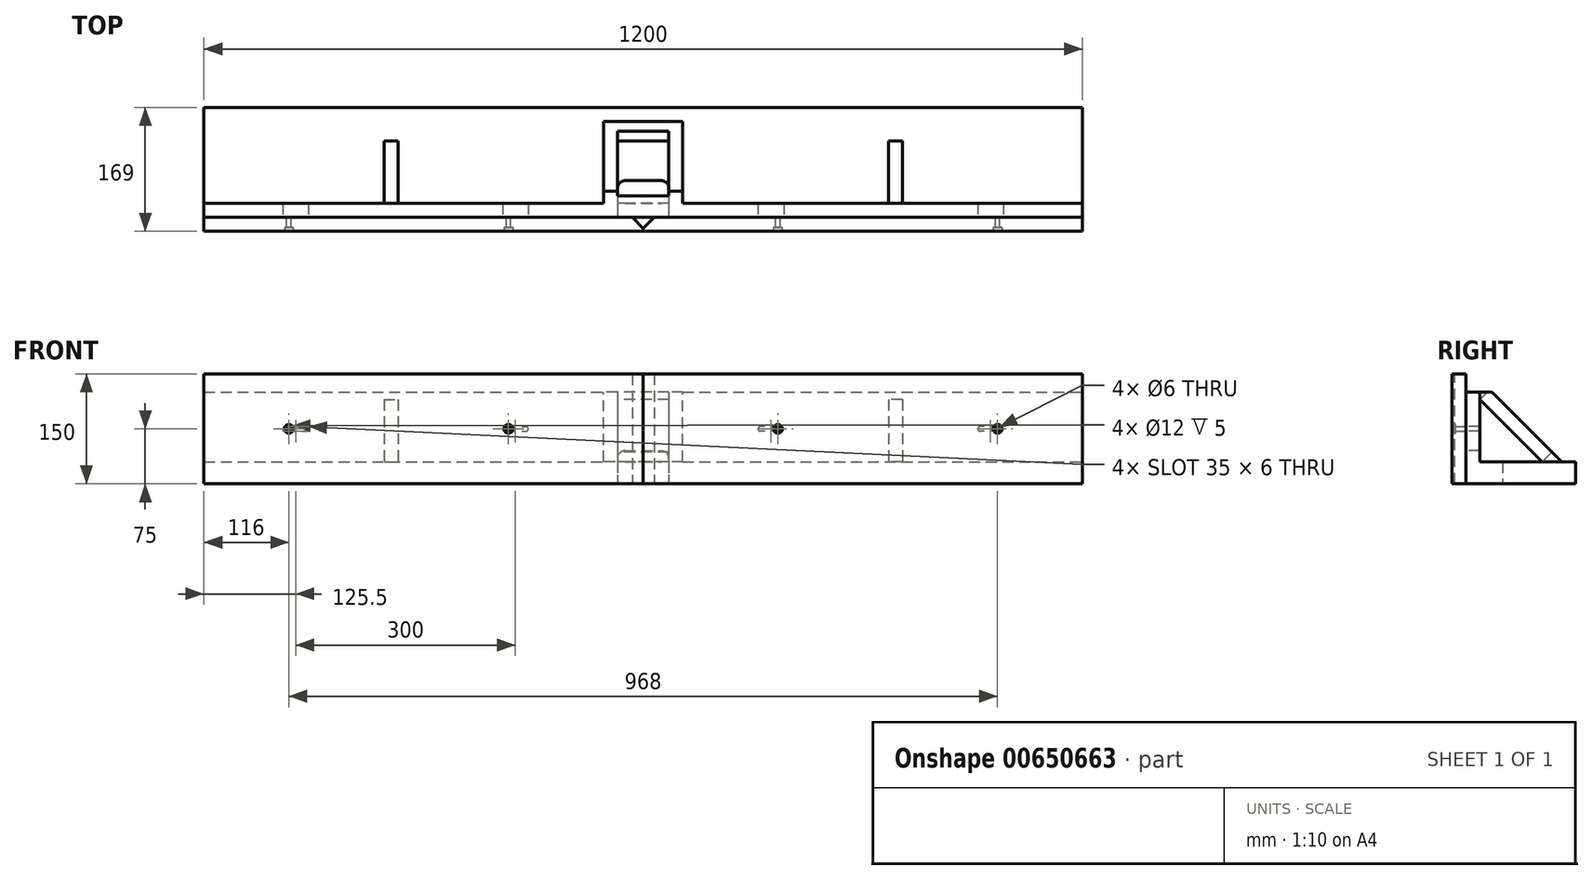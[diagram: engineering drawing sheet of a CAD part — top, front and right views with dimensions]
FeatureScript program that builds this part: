
annotation { "Feature Type Name" : "Feature", "Feature Type Description" : "" }
export const myFeature = defineFeature(function(context is Context, id is Id, definition is map)
    precondition{}
    {
        {
            var Q0;
            Q0=qCreatedBy(makeId("Front.planeOp"),FACE);
            var sketch = newSketch(context, id + "F0", { "sketchPlane" : qUnion([Q0])});
            skLineSegment(sketch, "E0.bottom", {"start": v(-600, 0) * mm, "end": v(600, 0) * mm});
            skLineSegment(sketch, "E0.top", {"start": v(-600, 125) * mm, "end": v(600, 125) * mm});
            skLineSegment(sketch, "E0.left", {"start": v(-600, 0) * mm, "end": v(-600, 125) * mm});
            skLineSegment(sketch, "E0.right", {"start": v(600, 0) * mm, "end": v(600, 125) * mm});
            skLineSegment(sketch, "E1.bottom", {"start": v(-25, 45) * mm, "end": v(25, 45) * mm});
            skLineSegment(sketch, "E1.top", {"start": v(-35, 0) * mm, "end": v(35, 0) * mm});
            skLineSegment(sketch, "E1.left", {"start": v(-35, 35) * mm, "end": v(-35, 0) * mm});
            skLineSegment(sketch, "E1.right", {"start": v(35, 35) * mm, "end": v(35, 0) * mm});
            skPoint(sketch, "E2.visualSharp", {"position": v(-35, 45) * mm});
            skArc(sketch, "E2.filletArc", {"start": v(-25, 45) * mm, "mid": v(-32.07, 42.07) * mm, "end": v(-35, 35) * mm});
            skPoint(sketch, "E3.visualSharp", {"position": v(35, 45) * mm});
            skArc(sketch, "E3.filletArc", {"start": v(35, 35) * mm, "mid": v(32.07, 42.07) * mm, "end": v(25, 45) * mm});
            skLineSegment(sketch, "E4", {"start": v(-574.08, 75) * mm, "end": v(534.24, 75) * mm, "construction": true});
            skLineSegment(sketch, "E5", {"start": v(-160, 105.56) * mm, "end": v(-160, 9.23) * mm, "construction": true});
            skLineSegment(sketch, "E6.bottom", {"start": v(-189, 78) * mm, "end": v(-160, 78) * mm});
            skLineSegment(sketch, "E6.top", {"start": v(-189, 72) * mm, "end": v(-160, 72) * mm});
            skLineSegment(sketch, "E6.left", {"start": v(-192, 75) * mm, "end": v(-192, 75) * mm});
            skLineSegment(sketch, "E6.right", {"start": v(-157, 75) * mm, "end": v(-157, 75) * mm});
            skPoint(sketch, "E7.visualSharp", {"position": v(-192, 78) * mm});
            skArc(sketch, "E7.filletArc", {"start": v(-189, 78) * mm, "mid": v(-191.12, 77.12) * mm, "end": v(-192, 75) * mm});
            skPoint(sketch, "E8.visualSharp", {"position": v(-192, 72) * mm});
            skArc(sketch, "E8.filletArc", {"start": v(-192, 75) * mm, "mid": v(-191.12, 72.88) * mm, "end": v(-189, 72) * mm});
            skPoint(sketch, "E9.visualSharp", {"position": v(-157, 78) * mm});
            skArc(sketch, "E9.filletArc", {"start": v(-157, 75) * mm, "mid": v(-157.88, 77.12) * mm, "end": v(-160, 78) * mm});
            skPoint(sketch, "E10.visualSharp", {"position": v(-157, 72) * mm});
            skArc(sketch, "E10.filletArc", {"start": v(-160, 72) * mm, "mid": v(-157.88, 72.88) * mm, "end": v(-157, 75) * mm});
            skPoint(sketch, "E11.1.0.0", {"position": v(-457, 78) * mm});
            skPoint(sketch, "E11.1.0.1", {"position": v(-492, 72) * mm});
            skLineSegment(sketch, "E11.1.0.2", {"start": v(-489, 78) * mm, "end": v(-460, 78) * mm});
            skPoint(sketch, "E11.1.0.3", {"position": v(-492, 78) * mm});
            skPoint(sketch, "E11.1.0.4", {"position": v(-457, 72) * mm});
            skLineSegment(sketch, "E11.1.0.5", {"start": v(-489, 72) * mm, "end": v(-460, 72) * mm});
            skArc(sketch, "E11.1.0.6", {"start": v(-492, 75) * mm, "mid": v(-491.12, 72.88) * mm, "end": v(-489, 72) * mm});
            skArc(sketch, "E11.1.0.7", {"start": v(-489, 78) * mm, "mid": v(-491.12, 77.12) * mm, "end": v(-492, 75) * mm});
            skArc(sketch, "E11.1.0.8", {"start": v(-457, 75) * mm, "mid": v(-457.88, 77.12) * mm, "end": v(-460, 78) * mm});
            skArc(sketch, "E11.1.0.9", {"start": v(-460, 72) * mm, "mid": v(-457.88, 72.88) * mm, "end": v(-457, 75) * mm});
            skLineSegment(sketch, "E11.direction1", {"start": v(-192, 72) * mm, "end": v(-492, 72) * mm, "construction": true});
            skArc(sketch, "E12.MirrorCS", {"start": v(157, 75) * mm, "mid": v(157.88, 77.12) * mm, "end": v(160, 78) * mm});
            skArc(sketch, "E13.MirrorCS", {"start": v(189, 78) * mm, "mid": v(191.12, 77.12) * mm, "end": v(192, 75) * mm});
            skArc(sketch, "E14.MirrorCS", {"start": v(160, 72) * mm, "mid": v(157.88, 72.88) * mm, "end": v(157, 75) * mm});
            skArc(sketch, "E15.MirrorCS", {"start": v(192, 75) * mm, "mid": v(191.12, 72.88) * mm, "end": v(189, 72) * mm});
            skPoint(sketch, "E16.MirrorP", {"position": v(192, 72) * mm});
            skPoint(sketch, "E17.MirrorP", {"position": v(192, 78) * mm});
            skLineSegment(sketch, "E18.MirrorCS", {"start": v(189, 72) * mm, "end": v(160, 72) * mm});
            skLineSegment(sketch, "E19.MirrorCS", {"start": v(189, 78) * mm, "end": v(160, 78) * mm});
            skPoint(sketch, "E20.MirrorP", {"position": v(157, 72) * mm});
            skPoint(sketch, "E21.MirrorP", {"position": v(157, 78) * mm});
            skArc(sketch, "E22.MirrorCS", {"start": v(457, 75) * mm, "mid": v(457.88, 77.12) * mm, "end": v(460, 78) * mm});
            skArc(sketch, "E23.MirrorCS", {"start": v(489, 78) * mm, "mid": v(491.12, 77.12) * mm, "end": v(492, 75) * mm});
            skArc(sketch, "E24.MirrorCS", {"start": v(492, 75) * mm, "mid": v(491.12, 72.88) * mm, "end": v(489, 72) * mm});
            skArc(sketch, "E25.MirrorCS", {"start": v(460, 72) * mm, "mid": v(457.88, 72.88) * mm, "end": v(457, 75) * mm});
            skPoint(sketch, "E26.MirrorP", {"position": v(457, 72) * mm});
            skPoint(sketch, "E27.MirrorP", {"position": v(492, 72) * mm});
            skLineSegment(sketch, "E28.MirrorCS", {"start": v(489, 72) * mm, "end": v(460, 72) * mm});
            skLineSegment(sketch, "E29.MirrorCS", {"start": v(489, 78) * mm, "end": v(460, 78) * mm});
            skPoint(sketch, "E30.MirrorP", {"position": v(492, 78) * mm});
            skPoint(sketch, "E31.MirrorP", {"position": v(457, 78) * mm});
            skSolve(sketch);
        }
        {
            var Q0;
            Q0=makeQuery(id+"F0.imprint","IMPRINT",FACE,{"disambiguationData":[TD([[makeQuery(id+"F0.imprint","IMPRINT",EDGE,{"derivedFrom":sQuery(id+"F0.wireOp",EDGE,"E0.top")}),-1.0]])]});
            extrude(context, id + "F1", {"entities" : qUnion([Q0]), "oppositeDirection" : true, "depth" : 19 * mm, "offsetDistance" : 25 * mm});
        }
        {
            var Q0;
            Q0=qCreatedBy(makeId("Top.planeOp"),FACE);
            var sketch = newSketch(context, id + "F2", { "sketchPlane" : qUnion([Q0])});
            skPoint(sketch, "E32.0", {"position": v(-600, 19) * mm});
            skLineSegment(sketch, "E33.bottom", {"start": v(-600, 19) * mm, "end": v(600, 19) * mm});
            skLineSegment(sketch, "E33.top", {"start": v(-600, 150) * mm, "end": v(600, 150) * mm});
            skLineSegment(sketch, "E33.left", {"start": v(-600, 19) * mm, "end": v(-600, 150) * mm});
            skLineSegment(sketch, "E33.right", {"start": v(600, 19) * mm, "end": v(600, 150) * mm});
            skPoint(sketch, "E34.0", {"position": v(600, 19) * mm});
            skPoint(sketch, "E35.0", {"position": v(600, 0) * mm});
            skLineSegment(sketch, "E36.0.0", {"start": v(-600, 0) * mm, "end": v(600, 0) * mm});
            skLineSegment(sketch, "E36.0.1", {"start": v(600, 0) * mm, "end": v(600, 19) * mm});
            skLineSegment(sketch, "E36.0.2", {"start": v(600, 19) * mm, "end": v(-600, 19) * mm});
            skLineSegment(sketch, "E36.0.3", {"start": v(-600, 19) * mm, "end": v(-600, 0) * mm});
            skLineSegment(sketch, "E37.bottom", {"start": v(-35, 19) * mm, "end": v(35, 19) * mm});
            skLineSegment(sketch, "E37.top", {"start": v(-25, 50) * mm, "end": v(25, 50) * mm});
            skLineSegment(sketch, "E37.left", {"start": v(-35, 19) * mm, "end": v(-35, 40) * mm});
            skLineSegment(sketch, "E37.right", {"start": v(35, 19) * mm, "end": v(35, 40) * mm});
            skPoint(sketch, "E38.visualSharp", {"position": v(-35, 50) * mm});
            skArc(sketch, "E38.filletArc", {"start": v(-25, 50) * mm, "mid": v(-32.07, 47.07) * mm, "end": v(-35, 40) * mm});
            skPoint(sketch, "E39.visualSharp", {"position": v(35, 50) * mm});
            skArc(sketch, "E39.filletArc", {"start": v(35, 40) * mm, "mid": v(32.07, 47.07) * mm, "end": v(25, 50) * mm});
            skLineSegment(sketch, "E40", {"start": v(-574.22, 90) * mm, "end": v(567.06, 90) * mm, "construction": true});
            skSolve(sketch);
        }
        {
            var Q0;
            Q0=makeQuery(id+"F2.imprint","IMPRINT",FACE,{"disambiguationData":[TD([[makeQuery(id+"F2.imprint","IMPRINT",EDGE,{"derivedFrom":sQuery(id+"F2.wireOp",EDGE,"E33.top")}),-1.0]])]});
            extrude(context, id + "F3", {"entities" : qUnion([Q0]), "depth" : 30 * mm, "offsetDistance" : 25 * mm});
        }
        {
            var Q0;
            Q0=makeQuery(id+"F3.opExtrude","SWEPT_FACE",FACE,{"disambiguationData":[OSD([sQuery(id+"F2.wireOp",EDGE,"E37.left")])]});
            var sketch = newSketch(context, id + "F4", { "sketchPlane" : qUnion([Q0])});
            skLineSegment(sketch, "E41", {"start": v(19, 115) * mm, "end": v(104, 30) * mm});
            skLineSegment(sketch, "E42.0", {"start": v(19, 30) * mm, "end": v(150, 30) * mm});
            skLineSegment(sketch, "E43", {"start": v(0, 0) * mm, "end": v(67, 67) * mm, "construction": true});
            skLineSegment(sketch, "E44.0", {"start": v(19, 0) * mm, "end": v(19, 125) * mm});
            skLineSegment(sketch, "E45", {"start": v(19, 115) * mm, "end": v(19, 30) * mm, "construction": true});
            skLineSegment(sketch, "E46", {"start": v(19, 30) * mm, "end": v(104, 30) * mm, "construction": true});
            skSolve(sketch);
        }
        {
            var Q0;
            {var subQ0=sQuery(id+"F4.wireOp",EDGE,"E41");Q0=makeQuery(id+"F4.imprint","IMPRINT",FACE,{"disambiguationData":[TD([[makeQuery(id+"F4.imprint","IMPRINT",EDGE,{"derivedFrom":subQ0}),-1.0]])]});}
            extrude(context, id + "F5", {"entities" : qUnion([Q0]), "oppositeDirection" : true, "depth" : 19 * mm, "offsetDistance" : 25 * mm});
        }
        {
            var Q0;
            Q0=makeQuery(id+"F5.opExtrude","SWEPT_BODY",BODY,{"disambiguationData":[OSD([sQuery(id+"F4.wireOp",EDGE,"E41"),sQuery(id+"F4.wireOp",EDGE,"E42.0"),sQuery(id+"F4.wireOp",EDGE,"E44.0")])]});
            var Q1;
            Q1=qCreatedBy(makeId("Right.planeOp"),FACE);
            mirror(context, id + "F6", {"entities" : qUnion([Q0]), "mirrorPlane" : qUnion([Q1])});
        }
        {
            var Q0;
            Q0=makeQuery(id+"F6.opPattern","COPY",FACE,{"derivedFrom":makeQuery(id+"F5.opExtrude","SWEPT_FACE",FACE,{"disambiguationData":[OSD([sQuery(id+"F4.wireOp",EDGE,"E41")])]}),"instanceName":"1"});
            var sketch = newSketch(context, id + "F7", { "sketchPlane" : qUnion([Q0])});
            skPoint(sketch, "E47.0", {"position": v(54, 67.88) * mm});
            skPoint(sketch, "E48.0", {"position": v(-54, -52.33) * mm});
            skLineSegment(sketch, "E49.bottom", {"start": v(54, 67.88) * mm, "end": v(-54, 67.88) * mm});
            skLineSegment(sketch, "E49.top", {"start": v(54, -52.33) * mm, "end": v(-54, -52.33) * mm});
            skLineSegment(sketch, "E49.left", {"start": v(54, 67.88) * mm, "end": v(54, -52.33) * mm});
            skLineSegment(sketch, "E49.right", {"start": v(-54, 67.88) * mm, "end": v(-54, -52.33) * mm});
            skLineSegment(sketch, "E50.0", {"start": v(35, 67.88) * mm, "end": v(35, -52.33) * mm});
            skLineSegment(sketch, "E50.1", {"start": v(35, 7.78) * mm, "end": v(35, -84.85) * mm});
            skLineSegment(sketch, "E50.3", {"start": v(35, -13.44) * mm, "end": v(35, 74.95) * mm});
            skLineSegment(sketch, "E50.4", {"start": v(35, 67.88) * mm, "end": v(35, 7.78) * mm});
            skLineSegment(sketch, "E50.5", {"start": v(35, 7.78) * mm, "end": v(35, -52.33) * mm});
            skLineSegment(sketch, "E51", {"start": v(-54, -52.33) * mm, "end": v(54, 67.88) * mm, "construction": true});
            skCircle(sketch, "E52", {"center": v(0, 7.78) * mm, "radius": 25 * mm});
            skSolve(sketch);
        }
        {
            var Q0;
            {var subQ2=sQuery(id+"F7.wireOp",EDGE,"E49.left");Q0=makeQuery(id+"F7.imprint","IMPRINT",FACE,{"disambiguationData":[TD([[makeQuery(id+"F7.imprint","IMPRINT",EDGE,{"derivedFrom":subQ2}),-1.0]])]});}
            var Q1;
            {var subQ2=sQuery(id+"F7.wireOp",EDGE,"E49.right");Q1=makeQuery(id+"F7.imprint","IMPRINT",FACE,{"disambiguationData":[TD([[makeQuery(id+"F7.imprint","IMPRINT",EDGE,{"derivedFrom":subQ2}),1.0]])]});}
            var Q2;
            {var subQ0=sQuery(id+"F7.wireOp",EDGE,"E50.4");Q2=makeQuery(id+"F7.imprint","IMPRINT",FACE,{"disambiguationData":[TD([[makeQuery(id+"F7.imprint","IMPRINT",EDGE,{"derivedFrom":subQ0}),-1.0]])]});}
            extrude(context, id + "F8", {"entities" : qUnion([Q0, Q1, Q2]), "depth" : 19 * mm, "offsetDistance" : 25 * mm});
        }
        {
            var Q0;
            Q0=makeQuery(id+"F6.opPattern","COPY",BODY,{"derivedFrom":makeQuery(id+"F5.opExtrude","SWEPT_BODY",BODY,{"disambiguationData":[OSD([sQuery(id+"F4.wireOp",EDGE,"E41"),sQuery(id+"F4.wireOp",EDGE,"E42.0"),sQuery(id+"F4.wireOp",EDGE,"E44.0")])]}),"instanceName":"1"});
            var Q1;
            Q1=makeQuery(id+"F3.opExtrude","SWEPT_FACE",FACE,{"disambiguationData":[OSD([sQuery(id+"F2.wireOp",EDGE,"E33.right")])]});
            transform(context, id + "F9", {"entities" : qUnion([Q0]), "transformType" : TransformType.TRANSLATION_DISTANCE, "transformDirection" : qUnion([Q1]), "distance" : 300 * mm, "makeCopy" : true});
        }
        {
            var Q0;
            Q0=makeQuery(id+"F5.opExtrude","SWEPT_BODY",BODY,{"disambiguationData":[OSD([sQuery(id+"F4.wireOp",EDGE,"E41"),sQuery(id+"F4.wireOp",EDGE,"E42.0"),sQuery(id+"F4.wireOp",EDGE,"E44.0")])]});
            var Q1;
            Q1=makeQuery(id+"F3.opExtrude","SWEPT_FACE",FACE,{"disambiguationData":[OSD([sQuery(id+"F2.wireOp",EDGE,"E33.left")])]});
            transform(context, id + "F10", {"entities" : qUnion([Q0]), "transformType" : TransformType.TRANSLATION_DISTANCE, "transformDirection" : qUnion([Q1]), "distance" : 300 * mm, "makeCopy" : true});
        }
        {
            var Q0;
            Q0=makeQuery(id+"F1.opExtrude","CAP_FACE",FACE,{"disambiguationData":[OSD([sQuery(id+"F0.wireOp",EDGE,"E0.bottom"),sQuery(id+"F0.wireOp",EDGE,"E0.top"),sQuery(id+"F0.wireOp",EDGE,"E0.left"),sQuery(id+"F0.wireOp",EDGE,"E0.right"),sQuery(id+"F0.wireOp",EDGE,"E1.bottom"),sQuery(id+"F0.wireOp",EDGE,"E1.left"),sQuery(id+"F0.wireOp",EDGE,"E1.right"),sQuery(id+"F0.wireOp",EDGE,"E2.filletArc"),sQuery(id+"F0.wireOp",EDGE,"E3.filletArc")])],"isStart":true});
            var sketch = newSketch(context, id + "F11", { "sketchPlane" : qUnion([Q0])});
            skPoint(sketch, "E53.oppositeSnap0", {"position": v(0, 125) * mm});
            skLineSegment(sketch, "E53.bottom", {"start": v(-600, 0) * mm, "end": v(0, 0) * mm});
            skLineSegment(sketch, "E53.top", {"start": v(-600, 150) * mm, "end": v(0, 150) * mm});
            skLineSegment(sketch, "E53.left", {"start": v(-600, 0) * mm, "end": v(-600, 150) * mm});
            skLineSegment(sketch, "E53.right", {"start": v(0, 0) * mm, "end": v(0, 150) * mm});
            skPoint(sketch, "E54.0", {"position": v(-492, 75) * mm});
            skLineSegment(sketch, "E55", {"start": v(-492, 75) * mm, "end": v(-484, 75) * mm, "construction": true});
            skCircle(sketch, "E56", {"center": v(-484, 75) * mm, "radius": 3 * mm});
            skPoint(sketch, "E57.0", {"position": v(-192, 75) * mm});
            skLineSegment(sketch, "E58", {"start": v(-192, 75) * mm, "end": v(-184, 75) * mm, "construction": true});
            skCircle(sketch, "E59", {"center": v(-184, 75) * mm, "radius": 3 * mm});
            skSolve(sketch);
        }
        {
            var Q0;
            {var subQ0=sQuery(id+"F11.wireOp",EDGE,"E53.top");Q0=makeQuery(id+"F11.imprint","IMPRINT",FACE,{"disambiguationData":[TD([[makeQuery(id+"F11.imprint","IMPRINT",EDGE,{"derivedFrom":subQ0}),-1.0]])]});}
            var Q1;
            Q1=makeQuery(id+"F11.imprint","IMPRINT",FACE,{"disambiguationData":[TD([[makeQuery(id+"F11.imprint","IMPRINT",EDGE,{"derivedFrom":sQuery(id+"F11.wireOp",EDGE,"5TplXbLe-atHF-5qlG-ofpx-RILVyFDyfBHe.bottom")}),1.0]])]});
            var Q2;
            {var subQ1=makeQuery(id+"F1.opExtrude","CAP_EDGE",EDGE,{"disambiguationData":[OSD([sQuery(id+"F0.wireOp",EDGE,"E1.left")])],"isStart":true});Q2=makeQuery(id+"F11.imprint","IMPRINT",FACE,{"disambiguationData":[TD([[makeQuery(id+"F11.imprint","IMPRINT",EDGE,{"derivedFrom":subQ1}),1.0]])]});}
            var Q3;
            {var subQ17=makeQuery(id+"F1.opExtrude","CAP_EDGE",EDGE,{"disambiguationData":[OSD([sQuery(id+"F0.wireOp",EDGE,"E1.left")])],"isStart":true});Q3=makeQuery(id+"F11.imprint","IMPRINT",FACE,{"disambiguationData":[TD([[makeQuery(id+"F11.imprint","IMPRINT",EDGE,{"derivedFrom":subQ17}),-1.0]])]});}
            var Q4;
            {var subQ5=makeQuery(id+"F1.opExtrude","CAP_EDGE",EDGE,{"disambiguationData":[OSD([sQuery(id+"F0.wireOp",EDGE,"E7.filletArc"),sQuery(id+"F0.wireOp",EDGE,"E8.filletArc")])],"isStart":true});Q4=makeQuery(id+"F11.imprint","IMPRINT",FACE,{"disambiguationData":[TD([[makeQuery(id+"F11.imprint","IMPRINT",EDGE,{"derivedFrom":subQ5}),1.0]])]});}
            var Q5;
            {var subQ5=makeQuery(id+"F1.opExtrude","CAP_EDGE",EDGE,{"disambiguationData":[OSD([sQuery(id+"F0.wireOp",EDGE,"E9.filletArc"),sQuery(id+"F0.wireOp",EDGE,"E10.filletArc")])],"isStart":true});Q5=makeQuery(id+"F11.imprint","IMPRINT",FACE,{"disambiguationData":[TD([[makeQuery(id+"F11.imprint","IMPRINT",EDGE,{"derivedFrom":subQ5}),1.0]])]});}
            var Q6;
            {var subQ5=makeQuery(id+"F1.opExtrude","CAP_EDGE",EDGE,{"disambiguationData":[OSD([sQuery(id+"F0.wireOp",EDGE,"E11.1.0.6"),sQuery(id+"F0.wireOp",EDGE,"E11.1.0.7")])],"isStart":true});Q6=makeQuery(id+"F11.imprint","IMPRINT",FACE,{"disambiguationData":[TD([[makeQuery(id+"F11.imprint","IMPRINT",EDGE,{"derivedFrom":subQ5}),1.0]])]});}
            var Q7;
            {var subQ5=makeQuery(id+"F1.opExtrude","CAP_EDGE",EDGE,{"disambiguationData":[OSD([sQuery(id+"F0.wireOp",EDGE,"E11.1.0.8"),sQuery(id+"F0.wireOp",EDGE,"E11.1.0.9")])],"isStart":true});Q7=makeQuery(id+"F11.imprint","IMPRINT",FACE,{"disambiguationData":[TD([[makeQuery(id+"F11.imprint","IMPRINT",EDGE,{"derivedFrom":subQ5}),1.0]])]});}
            extrude(context, id + "F12", {"entities" : qUnion([Q0, Q1, Q2, Q3, Q4, Q5, Q6, Q7]), "depth" : 19 * mm, "offsetDistance" : 25 * mm});
        }
        {
            var Q0;
            Q0=makeQuery(id+"F12.opExtrude","CAP_EDGE",EDGE,{"disambiguationData":[OSD([sQuery(id+"F11.wireOp",EDGE,"E53.right")])],"isStart":true});
            chamfer(context, id + "F13", {"entities" : qUnion([Q0]), "width" : 15 * mm, "tangentPropagation" : true});
        }
        {
            var Q0;
            Q0=makeQuery(id+"F12.opExtrude","CAP_FACE",FACE,{"disambiguationData":[OSD([sQuery(id+"F11.wireOp",EDGE,"E53.bottom"),sQuery(id+"F11.wireOp",EDGE,"E53.top"),sQuery(id+"F11.wireOp",EDGE,"E53.left"),sQuery(id+"F11.wireOp",EDGE,"E53.right"),sQuery(id+"F11.wireOp",EDGE,"E56"),sQuery(id+"F11.wireOp",EDGE,"E59")])],"isStart":false});
            var sketch = newSketch(context, id + "F14", { "sketchPlane" : qUnion([Q0])});
            skCircle(sketch, "E60.0", {"center": v(-484, 75) * mm, "radius": 3 * mm});
            skCircle(sketch, "E61.0", {"center": v(-184, 75) * mm, "radius": 3 * mm});
            skCircle(sketch, "E62", {"center": v(-484, 75) * mm, "radius": 6 * mm});
            skCircle(sketch, "E63", {"center": v(-184, 75) * mm, "radius": 6 * mm});
            skSolve(sketch);
        }
        {
            var Q0;
            Q0=makeQuery(id+"F14.imprint","IMPRINT",FACE,{"disambiguationData":[TD([[makeQuery(id+"F14.imprint","IMPRINT",EDGE,{"derivedFrom":sQuery(id+"F14.wireOp",EDGE,"E60.0")}),-1.0]])]});
            var Q1;
            Q1=makeQuery(id+"F14.imprint","IMPRINT",FACE,{"disambiguationData":[TD([[makeQuery(id+"F14.imprint","IMPRINT",EDGE,{"derivedFrom":sQuery(id+"F14.wireOp",EDGE,"E61.0")}),-1.0]])]});
            extrude(context, id + "F15", {"entities" : qUnion([Q0, Q1]), "operationType" : NewBodyOperationType.REMOVE, "oppositeDirection" : true, "depth" : 5 * mm, "offsetDistance" : 25 * mm});
        }
        {
            var Q0;
            Q0=makeQuery(id+"F12.opExtrude","SWEPT_BODY",BODY,{"disambiguationData":[OSD([sQuery(id+"F11.wireOp",EDGE,"E53.bottom"),sQuery(id+"F11.wireOp",EDGE,"E53.top"),sQuery(id+"F11.wireOp",EDGE,"E53.left"),sQuery(id+"F11.wireOp",EDGE,"E53.right"),sQuery(id+"F11.wireOp",EDGE,"E56"),sQuery(id+"F11.wireOp",EDGE,"E59")])]});
            var Q1;
            Q1=qCreatedBy(makeId("Right.planeOp"),FACE);
            mirror(context, id + "F16", {"entities" : qUnion([Q0]), "mirrorPlane" : qUnion([Q1])});
        }
        {
            var Q0;
            Q0=makeQuery(id+"F8.opExtrude","SWEPT_FACE",FACE,{"disambiguationData":[OSD([sQuery(id+"F7.wireOp",EDGE,"E49.left")])]});
            var sketch = newSketch(context, id + "F17", { "sketchPlane" : qUnion([Q0])});
            skPoint(sketch, "E64.0", {"position": v(-19, 125) * mm});
            skLineSegment(sketch, "E65", {"start": v(-19, 125) * mm, "end": v(-35.87, 125) * mm});
            skLineSegment(sketch, "E66", {"start": v(-117.44, 43.44) * mm, "end": v(-130.87, 30) * mm});
            skLineSegment(sketch, "E67.0", {"start": v(-19, 30) * mm, "end": v(-150, 30) * mm});
            skLineSegment(sketch, "E68.0", {"start": v(-32.44, 128.44) * mm, "end": v(-19, 115) * mm});
            skLineSegment(sketch, "E69.0", {"start": v(-19, 0) * mm, "end": v(-19, 125) * mm});
            skLineSegment(sketch, "E70.0", {"start": v(-32.44, 128.44) * mm, "end": v(-117.44, 43.44) * mm});
            skSolve(sketch);
        }
        {
            var Q0;
            {var subQ0=sQuery(id+"F17.wireOp",EDGE,"E70.0");var subQ1=sQuery(id+"F17.wireOp",EDGE,"E65");var subQ2=makeQuery(id+"F17.imprint","INTERSECT",VERTEX,{"derivedFrom":[subQ1,subQ0]});Q0=makeQuery(id+"F17.imprint","IMPRINT",FACE,{"disambiguationData":[TD([[makeQuery(id+"F17.imprint","IMPRINT",EDGE,{"disambiguationData":[TD([[subQ2,1.0]])],"derivedFrom":subQ1}),-1.0]])]});}
            var Q1;
            Q1=makeQuery(id+"F8.opExtrude","SWEPT_FACE",FACE,{"disambiguationData":[OSD([sQuery(id+"F7.wireOp",EDGE,"E49.right")])]});
            extrude(context, id + "F18", {"entities" : qUnion([Q0]), "operationType" : NewBodyOperationType.REMOVE, "endBound" : BoundingType.UP_TO_SURFACE, "oppositeDirection" : true, "depth" : 25 * mm, "endBoundEntityFace" : qUnion([Q1]), "offsetDistance" : 25 * mm});
        }
        {
            var Q0;
            {var subQ0=sQuery(id+"F17.wireOp",EDGE,"E66");Q0=makeQuery(id+"F17.imprint","IMPRINT",FACE,{"disambiguationData":[TD([[makeQuery(id+"F17.imprint","IMPRINT",EDGE,{"derivedFrom":subQ0}),1.0]])]});}
            var Q1;
            {var subQ0=sQuery(id+"F17.wireOp",EDGE,"E69.0");var subQ1=sQuery(id+"F17.wireOp",EDGE,"E65");var subQ2=makeQuery(id+"F17.imprint","INTERSECT",VERTEX,{"derivedFrom":[subQ1,subQ0]});Q1=makeQuery(id+"F17.imprint","IMPRINT",FACE,{"disambiguationData":[TD([[makeQuery(id+"F17.imprint","IMPRINT",EDGE,{"disambiguationData":[TD([[subQ2,-1.0]])],"derivedFrom":subQ1}),1.0]])]});}
            var Q2;
            Q2=makeQuery(id+"F8.opExtrude","SWEPT_FACE",FACE,{"disambiguationData":[OSD([sQuery(id+"F7.wireOp",EDGE,"E49.right")])]});
            extrude(context, id + "F19", {"entities" : qUnion([Q0, Q1]), "operationType" : NewBodyOperationType.ADD, "endBound" : BoundingType.UP_TO_SURFACE, "oppositeDirection" : true, "depth" : 25 * mm, "endBoundEntityFace" : qUnion([Q2]), "offsetDistance" : 25 * mm});
        }
    });
